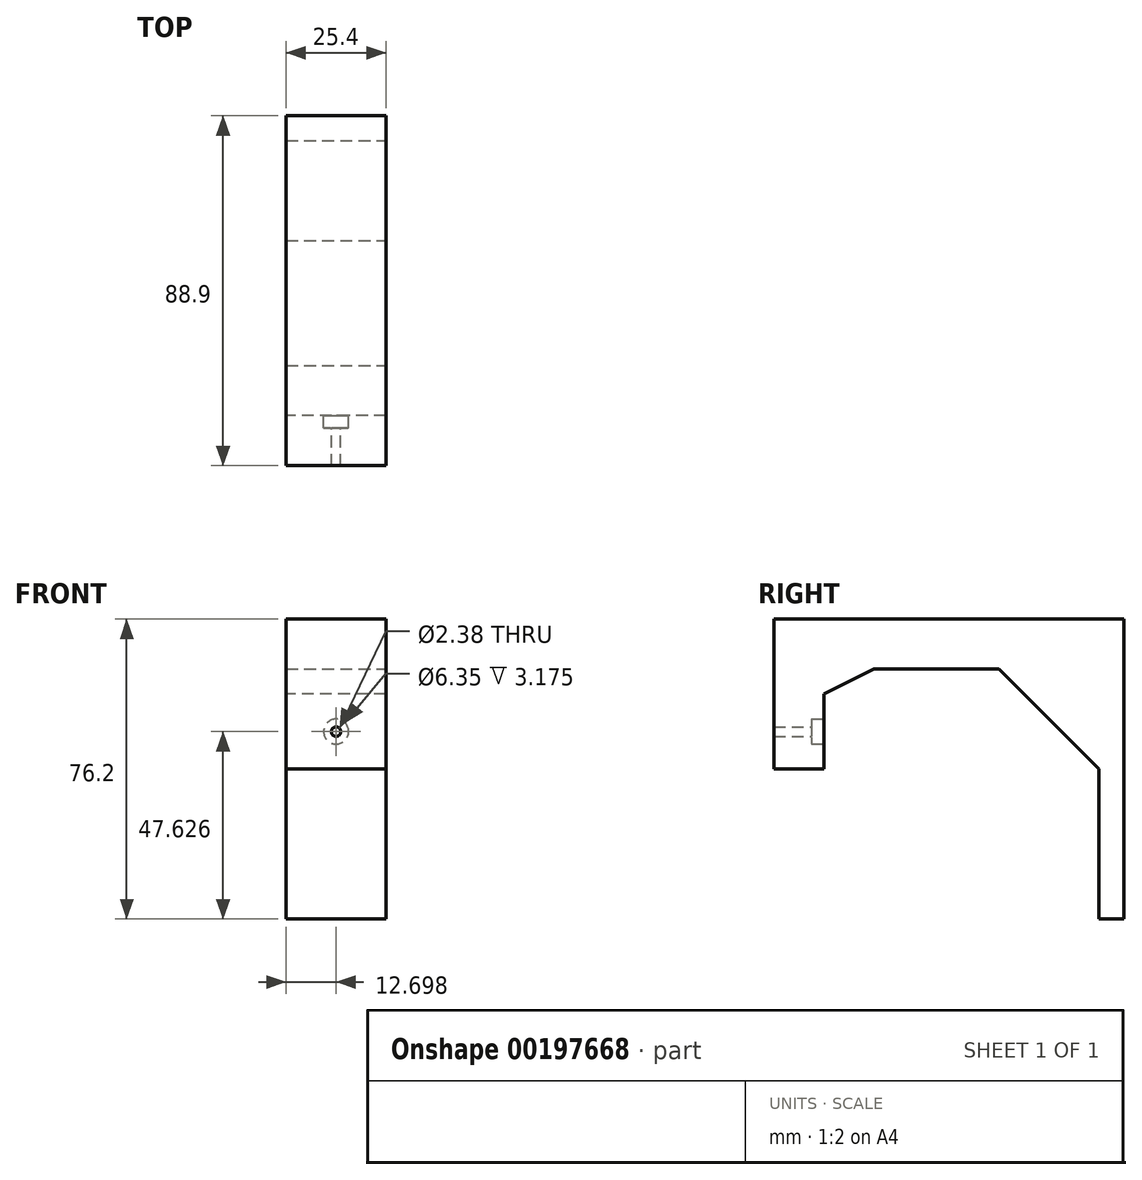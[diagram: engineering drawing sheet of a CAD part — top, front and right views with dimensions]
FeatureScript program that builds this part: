
annotation { "Feature Type Name" : "Feature", "Feature Type Description" : "" }
export const myFeature = defineFeature(function(context is Context, id is Id, definition is map)
    precondition{}
    {
        {
            var Q0;
            Q0=qCreatedBy(makeId("Front.planeOp"),FACE);
            var sketch = newSketch(context, id + "F0", { "sketchPlane" : qUnion([Q0])});
            skLineSegment(sketch, "E0.bottom", {"start": v(-33.36, 3.11) * mm, "end": v(-7.96, 3.11) * mm});
            skLineSegment(sketch, "E0.top", {"start": v(-33.36, -34.99) * mm, "end": v(-7.96, -34.99) * mm});
            skLineSegment(sketch, "E0.left", {"start": v(-33.36, 3.11) * mm, "end": v(-33.36, -34.99) * mm});
            skLineSegment(sketch, "E0.right", {"start": v(-7.96, 3.11) * mm, "end": v(-7.96, -34.99) * mm});
            skSolve(sketch);
        }
        {
            var Q0;
            Q0 = qSketchRegion(id + "F0", true);
            extrude(context, id + "F1", {"entities" : qUnion([Q0]), "oppositeDirection" : true, "depth" : 12.7 * mm});
        }
        {
            var Q0;
            Q0=makeQuery(id+"F1.opExtrude","CAP_FACE",FACE,{"disambiguationData":[OSD([sQuery(id+"F0.wireOp",EDGE,"E0.bottom"),sQuery(id+"F0.wireOp",EDGE,"E0.top"),sQuery(id+"F0.wireOp",EDGE,"E0.left"),sQuery(id+"F0.wireOp",EDGE,"E0.right")])],"isStart":false});
            var sketch = newSketch(context, id + "F2", { "sketchPlane" : qUnion([Q0])});
            skLineSegment(sketch, "E1", {"start": v(20.66, -9.59) * mm, "end": v(7.96, -9.59) * mm});
            skLineSegment(sketch, "E2", {"start": v(20.66, -9.59) * mm, "end": v(33.36, -9.59) * mm});
            skSolve(sketch);
        }
        {
            var Q0;
            {var subQ3=sQuery(id+"F2.wireOp",EDGE,"E1");Q0=makeQuery(id+"F2.imprint","IMPRINT",FACE,{"disambiguationData":[TD([[makeQuery(id+"F2.imprint","IMPRINT",EDGE,{"derivedFrom":subQ3}),-1.0]])]});}
            extrude(context, id + "F3", {"entities" : qUnion([Q0]), "operationType" : NewBodyOperationType.ADD, "depth" : 76.2 * mm});
        }
        {
            var Q0;
            Q0=makeQuery(id+"F3.opExtrude","SWEPT_FACE",FACE,{"disambiguationData":[OSD([sQuery(id+"F2.wireOp",EDGE,"E1"),sQuery(id+"F2.wireOp",EDGE,"E2")])]});
            var sketch = newSketch(context, id + "F4", { "sketchPlane" : qUnion([Q0])});
            skLineSegment(sketch, "E3.bottom", {"start": v(-7.96, -88.9) * mm, "end": v(-33.36, -88.9) * mm});
            skLineSegment(sketch, "E3.top", {"start": v(-7.96, -82.55) * mm, "end": v(-33.36, -82.55) * mm});
            skLineSegment(sketch, "E3.left", {"start": v(-7.96, -88.9) * mm, "end": v(-7.96, -82.55) * mm});
            skLineSegment(sketch, "E3.right", {"start": v(-33.36, -88.9) * mm, "end": v(-33.36, -82.55) * mm});
            skSolve(sketch);
        }
        {
            var Q0;
            Q0=makeQuery(id+"F4.imprint","IMPRINT",FACE,{"disambiguationData":[TD([[makeQuery(id+"F4.imprint","IMPRINT",EDGE,{"derivedFrom":sQuery(id+"F4.wireOp",EDGE,"E3.bottom")}),1.0]])]});
            extrude(context, id + "F5", {"entities" : qUnion([Q0]), "operationType" : NewBodyOperationType.ADD, "depth" : 63.5 * mm});
        }
        {
            var Q0;
            {var subQ0=sQuery(id+"F0.wireOp",EDGE,"E0.right");Q0=makeQuery(id+"F5.boolean.opBoolean","MERGE",FACE,{"derivedFrom":[makeQuery(id+"F3.boolean.opBoolean","MERGE",FACE,{"derivedFrom":[makeQuery(id+"F1.opExtrude","SWEPT_FACE",FACE,{"disambiguationData":[OSD([subQ0])]}),makeQuery(id+"F3.opExtrude","SWEPT_FACE",FACE,{"disambiguationData":[OSD([subQ0])]})]}),makeQuery(id+"F5.opExtrude","SWEPT_FACE",FACE,{"disambiguationData":[OSD([sQuery(id+"F4.wireOp",EDGE,"E3.left")])]})]});}
            var sketch = newSketch(context, id + "F6", { "sketchPlane" : qUnion([Q0])});
            skLineSegment(sketch, "E4", {"start": v(82.55, -34.99) * mm, "end": v(57.15, -9.59) * mm});
            skLineSegment(sketch, "E5", {"start": v(57.15, -9.59) * mm, "end": v(82.55, -9.59) * mm});
            skLineSegment(sketch, "E6", {"start": v(82.55, -9.59) * mm, "end": v(82.55, -34.99) * mm});
            skSolve(sketch);
        }
        {
            var Q0;
            Q0=makeQuery(id+"F6.imprint","IMPRINT",FACE,{"disambiguationData":[TD([[makeQuery(id+"F6.imprint","IMPRINT",EDGE,{"derivedFrom":sQuery(id+"F6.wireOp",EDGE,"E4")}),-1.0]])]});
            extrude(context, id + "F7", {"entities" : qUnion([Q0]), "operationType" : NewBodyOperationType.ADD, "oppositeDirection" : true, "depth" : 25.4 * mm});
        }
        {
            var Q0;
            Q0=makeQuery(id+"F1.opExtrude","CAP_FACE",FACE,{"disambiguationData":[OSD([sQuery(id+"F0.wireOp",EDGE,"E0.bottom"),sQuery(id+"F0.wireOp",EDGE,"E0.top"),sQuery(id+"F0.wireOp",EDGE,"E0.left"),sQuery(id+"F0.wireOp",EDGE,"E0.right")])],"isStart":false});
            var sketch = newSketch(context, id + "F8", { "sketchPlane" : qUnion([Q0])});
            skLineSegment(sketch, "E7", {"start": v(7.96, -9.59) * mm, "end": v(7.96, -15.94) * mm});
            skLineSegment(sketch, "E8.bottom", {"start": v(7.96, -9.59) * mm, "end": v(33.36, -9.59) * mm});
            skLineSegment(sketch, "E8.top", {"start": v(7.96, -15.94) * mm, "end": v(33.36, -15.94) * mm});
            skLineSegment(sketch, "E8.right", {"start": v(33.36, -9.59) * mm, "end": v(33.36, -15.94) * mm});
            skSolve(sketch);
        }
        {
            var Q0;
            Q0 = qSketchRegion(id + "F8", true);
            extrude(context, id + "F9", {"entities" : qUnion([Q0]), "operationType" : NewBodyOperationType.ADD, "depth" : 12.7 * mm});
        }
        {
            var Q0;
            {var subQ0=sQuery(id+"F0.wireOp",EDGE,"E0.right");Q0=makeQuery(id+"F9.boolean.opBoolean","MERGE",FACE,{"derivedFrom":[makeQuery(id+"F7.boolean.opBoolean","MERGE",FACE,{"derivedFrom":[makeQuery(id+"F5.boolean.opBoolean","MERGE",FACE,{"derivedFrom":[makeQuery(id+"F3.boolean.opBoolean","MERGE",FACE,{"derivedFrom":[makeQuery(id+"F1.opExtrude","SWEPT_FACE",FACE,{"disambiguationData":[OSD([subQ0])]}),makeQuery(id+"F3.opExtrude","SWEPT_FACE",FACE,{"disambiguationData":[OSD([subQ0])]})]}),makeQuery(id+"F5.opExtrude","SWEPT_FACE",FACE,{"disambiguationData":[OSD([sQuery(id+"F4.wireOp",EDGE,"E3.left")])]})]}),makeQuery(id+"F7.opExtrude","CAP_FACE",FACE,{"disambiguationData":[OSD([sQuery(id+"F6.wireOp",EDGE,"E4"),sQuery(id+"F6.wireOp",EDGE,"E5"),sQuery(id+"F6.wireOp",EDGE,"E6")])],"isStart":true})]}),makeQuery(id+"F9.opExtrude","SWEPT_FACE",FACE,{"disambiguationData":[OSD([sQuery(id+"F8.wireOp",EDGE,"E7")])]})]});}
            var sketch = newSketch(context, id + "F10", { "sketchPlane" : qUnion([Q0])});
            skLineSegment(sketch, "E9", {"start": v(25.4, -9.59) * mm, "end": v(12.7, -15.94) * mm});
            skSolve(sketch);
        }
        {
            var Q0;
            Q0=makeQuery(id+"F10.imprint","IMPRINT",FACE,{"disambiguationData":[TD([[makeQuery(id+"F10.imprint","IMPRINT",EDGE,{"derivedFrom":sQuery(id+"F10.wireOp",EDGE,"E9")}),1.0]])]});
            extrude(context, id + "F11", {"entities" : qUnion([Q0]), "operationType" : NewBodyOperationType.REMOVE, "endBound" : BoundingType.UP_TO_NEXT, "oppositeDirection" : true, "depth" : 25.4 * mm});
        }
        {
            var Q0;
            Q0=makeQuery(id+"F1.opExtrude","CAP_FACE",FACE,{"disambiguationData":[OSD([sQuery(id+"F0.wireOp",EDGE,"E0.bottom"),sQuery(id+"F0.wireOp",EDGE,"E0.top"),sQuery(id+"F0.wireOp",EDGE,"E0.left"),sQuery(id+"F0.wireOp",EDGE,"E0.right")])],"isStart":false});
            var sketch = newSketch(context, id + "F12", { "sketchPlane" : qUnion([Q0])});
            skLineSegment(sketch, "E10", {"start": v(7.96, -25.46) * mm, "end": v(33.36, -25.46) * mm, "construction": true});
            skLineSegment(sketch, "E11", {"start": v(20.66, -34.99) * mm, "end": v(20.66, -25.46) * mm, "construction": true});
            skSolve(sketch);
        }
        {
            var Q0;
            Q0=sQuery(id+"F12.wireOp",VERTEX,"E11.end");
            var Q1;
            Q1=makeQuery(id+"F1.opExtrude","SWEPT_BODY",BODY,{"disambiguationData":[OSD([sQuery(id+"F0.wireOp",EDGE,"E0.bottom"),sQuery(id+"F0.wireOp",EDGE,"E0.top"),sQuery(id+"F0.wireOp",EDGE,"E0.left"),sQuery(id+"F0.wireOp",EDGE,"E0.right")])]});
            hole(context, id + "F13", {"style" : HoleStyle.C_BORE, "endStyle" : HoleEndStyle.BLIND, "holeDiameter" : 2.38 * mm, "cBoreDiameter" : 6.35 * mm, "cBoreDepth" : 3.17 * mm, "holeDepth" : 12.7 * mm, "locations" : qUnion([Q0]), "scope" : qUnion([Q1])});
        }
    });
